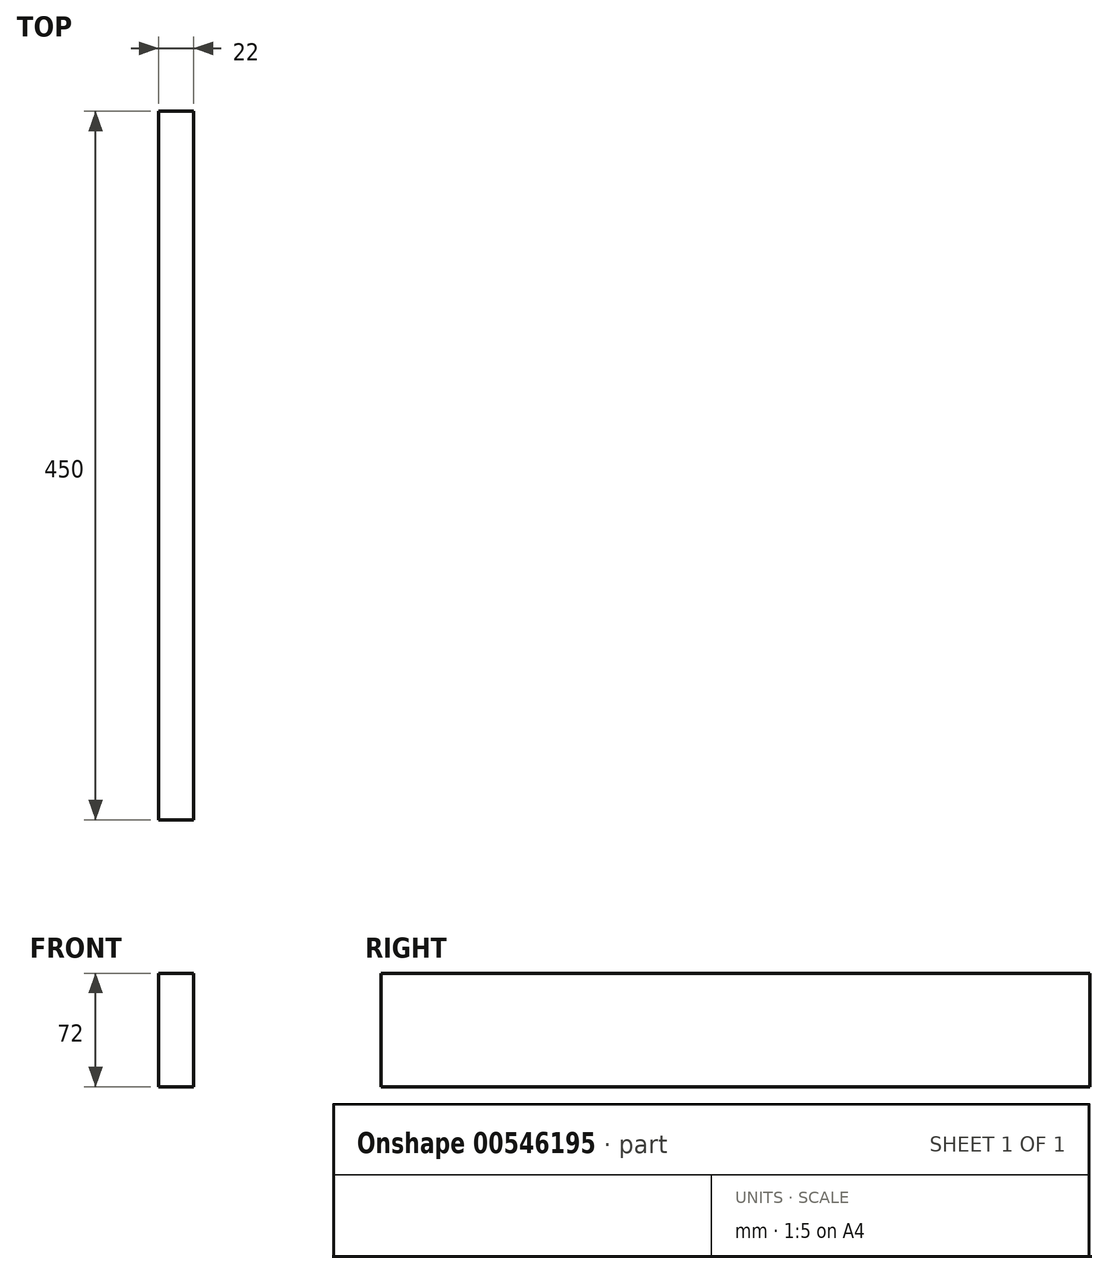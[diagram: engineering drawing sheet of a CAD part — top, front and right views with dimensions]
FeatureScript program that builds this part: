
annotation { "Feature Type Name" : "Feature", "Feature Type Description" : "" }
export const myFeature = defineFeature(function(context is Context, id is Id, definition is map)
    precondition{}
    {
        {
            var Q0;
            Q0=qCreatedBy(makeId("Top.planeOp"),FACE);
            var sketch = newSketch(context, id + "F0", { "sketchPlane" : qUnion([Q0])});
            skLineSegment(sketch, "E0.bottom", {"start": v(0, 0) * mm, "end": v(22, 0) * mm});
            skLineSegment(sketch, "E0.top", {"start": v(0, 450) * mm, "end": v(22, 450) * mm});
            skLineSegment(sketch, "E0.left", {"start": v(0, 0) * mm, "end": v(0, 450) * mm});
            skLineSegment(sketch, "E0.right", {"start": v(22, 0) * mm, "end": v(22, 450) * mm});
            skSolve(sketch);
        }
        {
            var Q0;
            Q0 = qSketchRegion(id + "F0", true);
            extrude(context, id + "F1", {"entities" : qUnion([Q0]), "depth" : 72 * mm, "offsetDistance" : 25 * mm});
        }
    });
